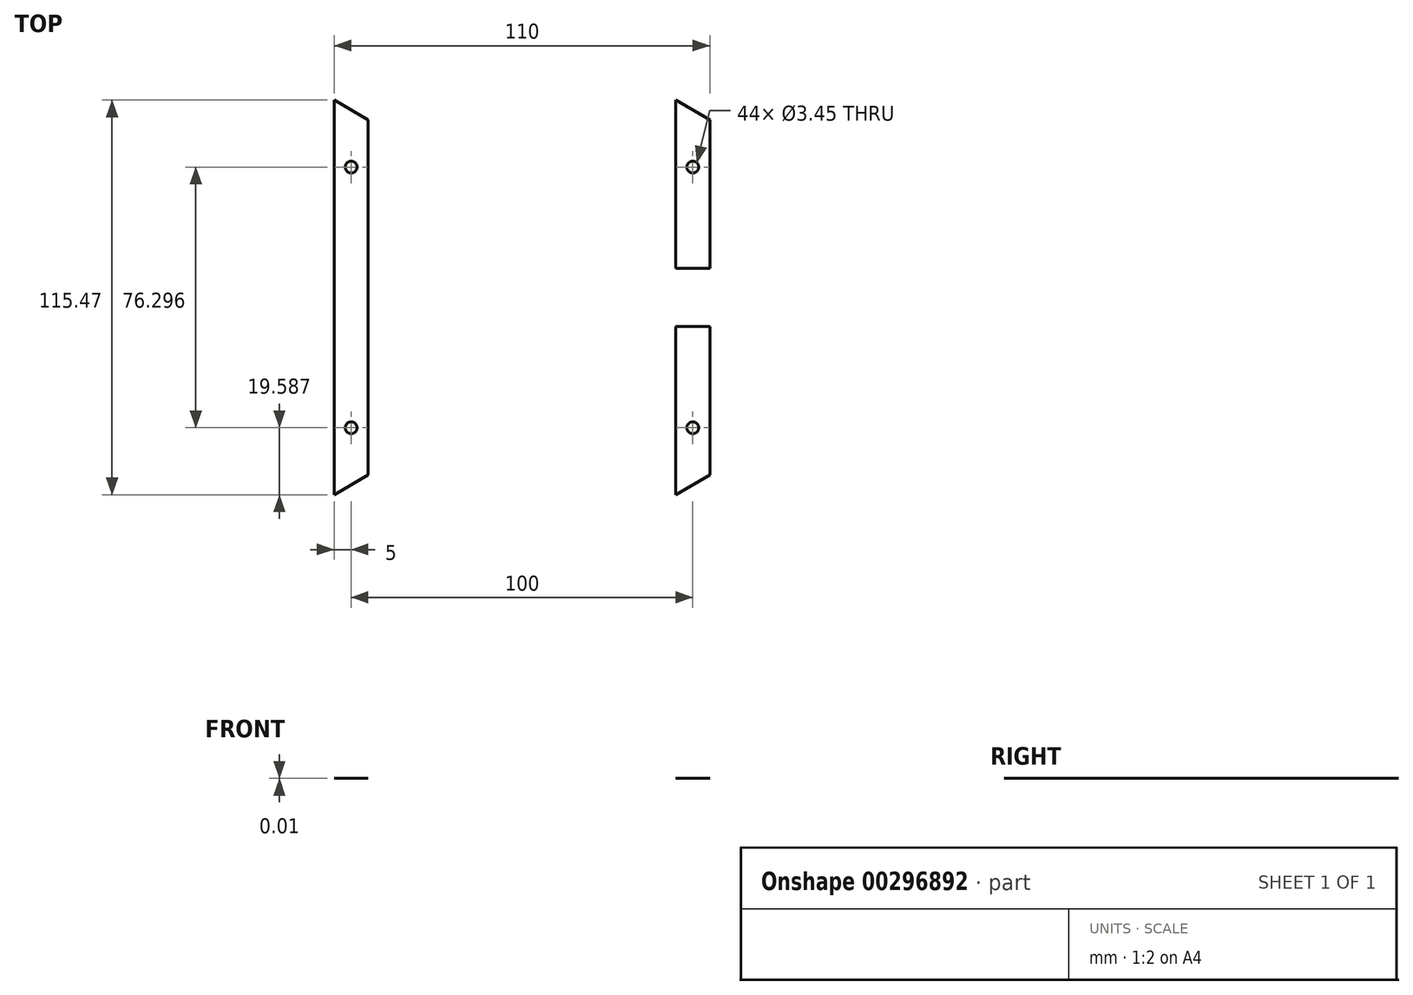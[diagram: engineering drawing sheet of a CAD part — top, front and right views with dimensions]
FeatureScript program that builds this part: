
annotation { "Feature Type Name" : "Feature", "Feature Type Description" : "" }
export const myFeature = defineFeature(function(context is Context, id is Id, definition is map)
    precondition{}
    {
        {
            var Q0;
            Q0=qCreatedBy(makeId("Top.planeOp"),FACE);
            var sketch = newSketch(context, id + "F0", { "sketchPlane" : qUnion([Q0])});
            skLineSegment(sketch, "E0", {"start": v(0, 0) * mm, "end": v(0, 115.47) * mm});
            skLineSegment(sketch, "E1", {"start": v(0, 115.47) * mm, "end": v(10, 109.7) * mm});
            skLineSegment(sketch, "E2", {"start": v(10, 109.7) * mm, "end": v(10, 5.77) * mm});
            skLineSegment(sketch, "E3", {"start": v(10, 5.77) * mm, "end": v(0, 0) * mm});
            skCircle(sketch, "E4", {"center": v(5, 95.88) * mm, "radius": 1.73 * mm});
            skCircle(sketch, "E5", {"center": v(5, 19.59) * mm, "radius": 1.73 * mm});
            skLineSegment(sketch, "E6", {"start": v(5, 95.88) * mm, "end": v(5, 19.59) * mm, "construction": true});
            skLineSegment(sketch, "E7", {"start": v(5, 95.88) * mm, "end": v(10, 95.88) * mm, "construction": true});
            skLineSegment(sketch, "E8", {"start": v(5, 95.88) * mm, "end": v(0, 95.88) * mm, "construction": true});
            skLineSegment(sketch, "E9", {"start": v(5, 112.58) * mm, "end": v(5, 95.88) * mm, "construction": true});
            skLineSegment(sketch, "E10", {"start": v(5, 19.59) * mm, "end": v(5, 2.89) * mm, "construction": true});
            skLineSegment(sketch, "E11", {"start": v(0, 0) * mm, "end": v(100, 0) * mm, "construction": true});
            skLineSegment(sketch, "E12", {"start": v(100, 0) * mm, "end": v(100, 49.23) * mm});
            skLineSegment(sketch, "E13", {"start": v(100, 115.47) * mm, "end": v(110, 109.7) * mm});
            skLineSegment(sketch, "E14", {"start": v(110, 109.7) * mm, "end": v(110, 66.23) * mm});
            skLineSegment(sketch, "E15", {"start": v(110, 5.77) * mm, "end": v(100, 0) * mm});
            skCircle(sketch, "E16", {"center": v(105, 95.88) * mm, "radius": 1.73 * mm});
            skCircle(sketch, "E17", {"center": v(105, 19.59) * mm, "radius": 1.73 * mm});
            skLineSegment(sketch, "E18", {"start": v(105, 95.88) * mm, "end": v(105, 19.59) * mm, "construction": true});
            skLineSegment(sketch, "E19", {"start": v(105, 95.88) * mm, "end": v(110, 95.88) * mm, "construction": true});
            skLineSegment(sketch, "E20", {"start": v(105, 95.88) * mm, "end": v(100, 95.88) * mm, "construction": true});
            skLineSegment(sketch, "E21", {"start": v(105, 112.58) * mm, "end": v(105, 95.88) * mm, "construction": true});
            skLineSegment(sketch, "E22", {"start": v(105, 19.59) * mm, "end": v(105, 2.89) * mm, "construction": true});
            skLineSegment(sketch, "E23", {"start": v(110, 66.23) * mm, "end": v(100, 66.23) * mm});
            skLineSegment(sketch, "E24", {"start": v(100, 49.23) * mm, "end": v(110, 49.23) * mm});
            skLineSegment(sketch, "E25.trimOffspring", {"start": v(100, 66.23) * mm, "end": v(100, 115.47) * mm});
            skLineSegment(sketch, "E26.trimOffspring", {"start": v(110, 49.23) * mm, "end": v(110, 5.77) * mm});
            skLineSegment(sketch, "E27", {"start": v(200, 0) * mm, "end": v(200, 115.47) * mm});
            skLineSegment(sketch, "E28", {"start": v(200, 115.47) * mm, "end": v(210, 109.7) * mm});
            skLineSegment(sketch, "E29", {"start": v(210, 109.7) * mm, "end": v(210, 5.77) * mm});
            skLineSegment(sketch, "E30", {"start": v(210, 5.77) * mm, "end": v(200, 0) * mm});
            skCircle(sketch, "E31", {"center": v(205, 95.88) * mm, "radius": 1.73 * mm});
            skCircle(sketch, "E32", {"center": v(205, 19.59) * mm, "radius": 1.73 * mm});
            skLineSegment(sketch, "E33", {"start": v(205, 95.88) * mm, "end": v(205, 19.59) * mm, "construction": true});
            skLineSegment(sketch, "E34", {"start": v(205, 95.88) * mm, "end": v(210, 95.88) * mm, "construction": true});
            skLineSegment(sketch, "E35", {"start": v(205, 95.88) * mm, "end": v(200, 95.88) * mm, "construction": true});
            skLineSegment(sketch, "E36", {"start": v(205, 112.58) * mm, "end": v(205, 95.88) * mm, "construction": true});
            skLineSegment(sketch, "E37", {"start": v(205, 19.59) * mm, "end": v(205, 2.89) * mm, "construction": true});
            skLineSegment(sketch, "E38", {"start": v(200, 0) * mm, "end": v(100, 0) * mm, "construction": true});
            skSolve(sketch);
        }
        {
            var Q0;
            Q0=makeQuery(id+"F0.imprint","IMPRINT",FACE,{"disambiguationData":[TD([[makeQuery(id+"F0.imprint","IMPRINT",EDGE,{"derivedFrom":sQuery(id+"F0.wireOp",EDGE,"E0")}),-1.0]])]});
            var Q1;
            Q1=makeQuery(id+"F0.imprint","IMPRINT",FACE,{"disambiguationData":[TD([[makeQuery(id+"F0.imprint","IMPRINT",EDGE,{"derivedFrom":sQuery(id+"F0.wireOp",EDGE,"E12")}),-1.0]])]});
            var Q2;
            Q2=makeQuery(id+"F0.imprint","IMPRINT",FACE,{"disambiguationData":[TD([[makeQuery(id+"F0.imprint","IMPRINT",EDGE,{"derivedFrom":sQuery(id+"F0.wireOp",EDGE,"E13")}),-1.0]])]});
            extrude(context, id + "F1", {"entities" : qUnion([Q0, Q1, Q2]), "depth" : 1 / 101.6 * mm});
        }
    });
